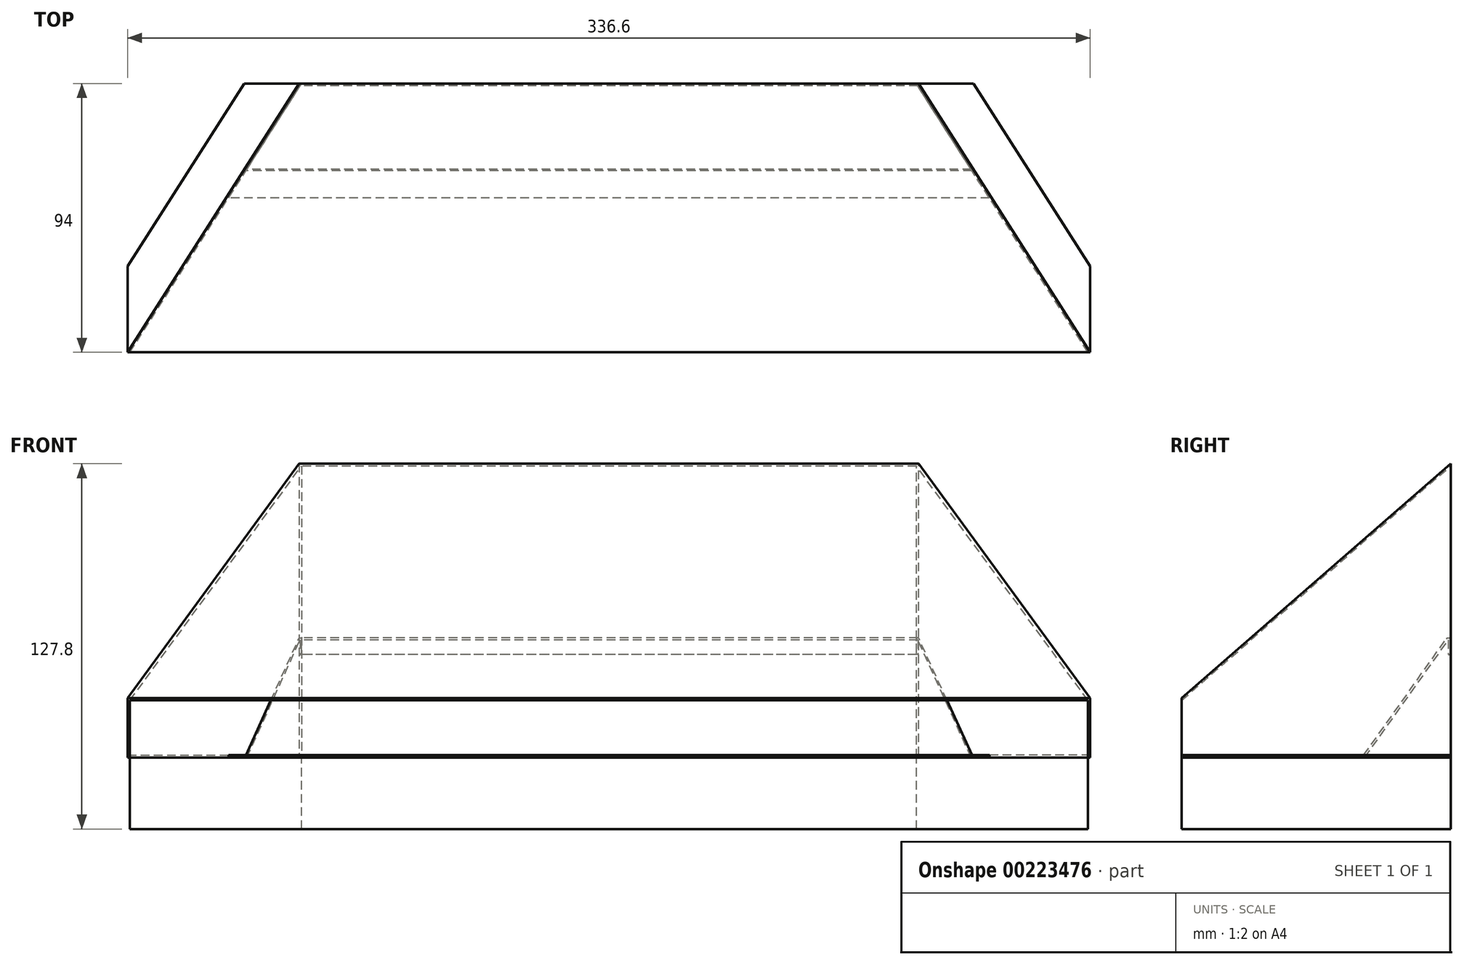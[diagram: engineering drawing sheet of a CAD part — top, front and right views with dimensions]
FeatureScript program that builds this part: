
annotation { "Feature Type Name" : "Feature", "Feature Type Description" : "" }
export const myFeature = defineFeature(function(context is Context, id is Id, definition is map)
    precondition{}
    {
        {
            var Q0;
            Q0=qCreatedBy(makeId("Front.planeOp"),FACE);
            var sketch = newSketch(context, id + "F0", { "sketchPlane" : qUnion([Q0])});
            skLineSegment(sketch, "E0.top", {"start": v(-167.5, 20) * mm, "end": v(167.5, 20) * mm});
            skLineSegment(sketch, "E0.left", {"start": v(-167.5, 0) * mm, "end": v(-167.5, 20) * mm});
            skLineSegment(sketch, "E0.right", {"start": v(167.5, 0) * mm, "end": v(167.5, 20) * mm});
            skLineSegment(sketch, "E1", {"start": v(-167.5, 0) * mm, "end": v(-187.5, 0) * mm});
            skLineSegment(sketch, "E2", {"start": v(167.5, 0) * mm, "end": v(187.5, 0) * mm});
            skLineSegment(sketch, "E3.0", {"start": v(-168.3, 0.8) * mm, "end": v(-187.5, 0.8) * mm});
            skLineSegment(sketch, "E3.1", {"start": v(168.3, 0.8) * mm, "end": v(187.5, 0.8) * mm});
            skLineSegment(sketch, "E3.2", {"start": v(168.3, 0.8) * mm, "end": v(168.3, 20.8) * mm});
            skLineSegment(sketch, "E3.3", {"start": v(-168.3, 20.8) * mm, "end": v(168.3, 20.8) * mm});
            skLineSegment(sketch, "E3.4", {"start": v(-168.3, 0.8) * mm, "end": v(-168.3, 20.8) * mm});
            skLineSegment(sketch, "E4", {"start": v(-187.5, 0.8) * mm, "end": v(-187.5, 0) * mm});
            skLineSegment(sketch, "E5", {"start": v(187.5, 0.8) * mm, "end": v(187.5, 0) * mm});
            skLineSegment(sketch, "E6.bottom", {"start": v(189, 0) * mm, "end": v(-189, 0) * mm, "construction": true});
            skLineSegment(sketch, "E6.top", {"start": v(189, 200.63) * mm, "end": v(-189, 200.63) * mm, "construction": true});
            skLineSegment(sketch, "E6.left", {"start": v(189, 0) * mm, "end": v(189, 200.63) * mm, "construction": true});
            skLineSegment(sketch, "E6.right", {"start": v(-189, 0) * mm, "end": v(-189, 200.63) * mm, "construction": true});
            skPoint(sketch, "E6.middle", {"position": v(0, 100.31) * mm});
            skSolve(sketch);
        }
        {
            var Q0;
            Q0=qCreatedBy(makeId("Right.planeOp"),FACE);
            var sketch = newSketch(context, id + "F1", { "sketchPlane" : qUnion([Q0])});
            skLineSegment(sketch, "E7", {"start": v(0, 0) * mm, "end": v(94, 0) * mm, "construction": true});
            skSolve(sketch);
        }
        {
            var Q0;
            Q0=sQuery(id+"F1.wireOp",VERTEX,"E7.end");
            var Q1;
            Q1=qCreatedBy(makeId("Front.planeOp"),FACE);
            cPlane(context, id + "F2", {"entities" : qUnion([Q0, Q1]), "cplaneType" : CPlaneType.PLANE_POINT, "offset" : 25 * mm, "width" : 150 * mm, "height" : 150 * mm});
        }
        {
            var Q0;
            Q0=qCreatedBy(id+"F2.planeOp",FACE);
            var sketch = newSketch(context, id + "F3", { "sketchPlane" : qUnion([Q0])});
            skLineSegment(sketch, "E8", {"start": v(127.5, 0) * mm, "end": v(107.5, 0) * mm});
            skLineSegment(sketch, "E9", {"start": v(107.5, 0) * mm, "end": v(107.5, 102) * mm});
            skLineSegment(sketch, "E10", {"start": v(107.5, 102) * mm, "end": v(-107.5, 102) * mm});
            skLineSegment(sketch, "E11", {"start": v(-107.5, 102) * mm, "end": v(-107.5, 0) * mm});
            skLineSegment(sketch, "E12", {"start": v(-107.5, 0) * mm, "end": v(-127.5, 0) * mm});
            skLineSegment(sketch, "E13.0", {"start": v(-108.3, 0.8) * mm, "end": v(-127.5, 0.8) * mm});
            skLineSegment(sketch, "E13.1", {"start": v(127.5, 0.8) * mm, "end": v(108.3, 0.8) * mm});
            skLineSegment(sketch, "E13.2", {"start": v(108.3, 0.8) * mm, "end": v(108.3, 102.8) * mm});
            skLineSegment(sketch, "E13.3", {"start": v(108.3, 102.8) * mm, "end": v(-108.3, 102.8) * mm});
            skLineSegment(sketch, "E13.4", {"start": v(-108.3, 102.8) * mm, "end": v(-108.3, 0.8) * mm});
            skLineSegment(sketch, "E14", {"start": v(-127.5, 0.81) * mm, "end": v(-127.5, 0) * mm});
            skLineSegment(sketch, "E15", {"start": v(127.5, 0.8) * mm, "end": v(127.5, 0) * mm});
            skSolve(sketch);
        }
        {
            var Q0;
            Q0=makeQuery(id+"F0.imprint","IMPRINT",FACE,{"disambiguationData":[TD([[makeQuery(id+"F0.imprint","IMPRINT",EDGE,{"derivedFrom":sQuery(id+"F0.wireOp",EDGE,"E0.top")}),1.0]])]});
            var Q1;
            Q1=makeQuery(id+"F3.imprint","IMPRINT",FACE,{"disambiguationData":[TD([[makeQuery(id+"F3.imprint","IMPRINT",EDGE,{"derivedFrom":sQuery(id+"F3.wireOp",EDGE,"E8")}),-1.0]])]});
            loft(context, id + "F4", {"sheetProfilesArray" : [{ "sheetProfileEntities" : qUnion([Q0]) }, { "sheetProfileEntities" : qUnion([Q1]) }]});
        }
        {
            var Q0;
            Q0=makeQuery(id+"F4.opLoft","SWEPT_FACE",FACE,{"disambiguationData":[OSD([sQuery(id+"F0.wireOp",EDGE,"E3.2"),sQuery(id+"F0.wireOp",EDGE,"E3.3"),sQuery(id+"F0.wireOp",EDGE,"E3.4"),sQuery(id+"F3.wireOp",EDGE,"E13.2"),sQuery(id+"F3.wireOp",EDGE,"E13.3"),sQuery(id+"F3.wireOp",EDGE,"E13.4")])]});
            var sketch = newSketch(context, id + "F5", { "sketchPlane" : qUnion([Q0])});
            skLineSegment(sketch, "E16.0", {"start": v(-168.3, 13.67) * mm, "end": v(-108.3, 138.41) * mm});
            skLineSegment(sketch, "E16.1", {"start": v(-168.3, 13.67) * mm, "end": v(168.3, 13.67) * mm});
            skLineSegment(sketch, "E16.2", {"start": v(168.3, 13.67) * mm, "end": v(108.3, 138.41) * mm});
            skLineSegment(sketch, "E16.3", {"start": v(-108.3, 138.41) * mm, "end": v(108.3, 138.41) * mm});
            skSolve(sketch);
        }
        {
            var Q0;
            Q0=makeQuery(id+"F4.opLoft","SWEPT_FACE",FACE,{"disambiguationData":[OSD([sQuery(id+"F0.wireOp",EDGE,"E3.0"),sQuery(id+"F0.wireOp",EDGE,"E3.4"),sQuery(id+"F0.wireOp",EDGE,"E4"),sQuery(id+"F3.wireOp",EDGE,"E13.0"),sQuery(id+"F3.wireOp",EDGE,"E13.4"),sQuery(id+"F3.wireOp",EDGE,"E14")])]});
            var sketch = newSketch(context, id + "F6", { "sketchPlane" : qUnion([Q0])});
            skLineSegment(sketch, "E17", {"start": v(-168.3, 0) * mm, "end": v(-168.3, 30.08) * mm});
            skLineSegment(sketch, "E18.0", {"start": v(168.3, 0) * mm, "end": v(187.5, 0) * mm});
            skLineSegment(sketch, "E18.1", {"start": v(187.5, 0) * mm, "end": v(127.5, 94) * mm});
            skLineSegment(sketch, "E18.2", {"start": v(168.3, 0) * mm, "end": v(108.3, 94) * mm});
            skLineSegment(sketch, "E19", {"start": v(168.3, 0) * mm, "end": v(168.3, 30.08) * mm});
            skSolve(sketch);
        }
        {
            var Q0;
            {var subQ0=sQuery(id+"F6.wireOp",EDGE,"E17");Q0=makeQuery(id+"F6.imprint","IMPRINT",FACE,{"disambiguationData":[TD([[makeQuery(id+"F6.imprint","IMPRINT",EDGE,{"derivedFrom":subQ0}),1.0]])]});}
            var Q1;
            {var subQ0=sQuery(id+"F6.wireOp",EDGE,"E18.0");Q1=makeQuery(id+"F6.imprint","IMPRINT",FACE,{"disambiguationData":[TD([[makeQuery(id+"F6.imprint","IMPRINT",EDGE,{"derivedFrom":subQ0}),1.0]])]});}
            extrude(context, id + "F7", {"entities" : qUnion([Q0, Q1]), "operationType" : NewBodyOperationType.REMOVE, "endBound" : BoundingType.THROUGH_ALL, "oppositeDirection" : true, "depth" : 25 * mm});
        }
        {
            var Q0;
            Q0=makeQuery(id+"F4.opLoft","SWEPT_FACE",FACE,{"disambiguationData":[OSD([sQuery(id+"F0.wireOp",EDGE,"E3.0"),sQuery(id+"F0.wireOp",EDGE,"E3.3"),sQuery(id+"F0.wireOp",EDGE,"E3.4"),sQuery(id+"F3.wireOp",EDGE,"E13.0"),sQuery(id+"F3.wireOp",EDGE,"E13.3"),sQuery(id+"F3.wireOp",EDGE,"E13.4")])]});
            var sketch = newSketch(context, id + "F8", { "sketchPlane" : qUnion([Q0])});
            skLineSegment(sketch, "E20.0", {"start": v(90.55, 20.8) * mm, "end": v(-20.97, 102.8) * mm});
            skLineSegment(sketch, "E20.1", {"start": v(90.55, 0.8) * mm, "end": v(90.55, 20.8) * mm});
            skLineSegment(sketch, "E20.2", {"start": v(-20.97, 0.8) * mm, "end": v(-20.97, 102.8) * mm});
            skLineSegment(sketch, "E20.3", {"start": v(90.55, 0.8) * mm, "end": v(-20.97, 0.8) * mm});
            skSolve(sketch);
        }
        {
            var Q0;
            Q0=qCreatedBy(makeId("Right.planeOp"),FACE);
            var sketch = newSketch(context, id + "F9", { "sketchPlane" : qUnion([Q0])});
            skLineSegment(sketch, "E21", {"start": v(93.2, 41.13) * mm, "end": v(64, 0) * mm});
            skLineSegment(sketch, "E22", {"start": v(64, 0) * mm, "end": v(54, 0) * mm});
            skLineSegment(sketch, "E23.0", {"start": v(63.59, 0.8) * mm, "end": v(54, 0.8) * mm});
            skLineSegment(sketch, "E23.1", {"start": v(92.55, 41.6) * mm, "end": v(63.59, 0.8) * mm});
            skLineSegment(sketch, "E24", {"start": v(54, 0.8) * mm, "end": v(54, 0) * mm});
            skPoint(sketch, "E25.orphan", {"position": v(94, 0.8) * mm});
            skPoint(sketch, "E26.orphan", {"position": v(94, 102.8) * mm});
            skLineSegment(sketch, "E27", {"start": v(94, 41.13) * mm, "end": v(94, 36.1) * mm});
            skLineSegment(sketch, "E28", {"start": v(94, 36.1) * mm, "end": v(93.2, 36.1) * mm});
            skLineSegment(sketch, "E29", {"start": v(93.2, 36.1) * mm, "end": v(93.2, 41.13) * mm});
            skPoint(sketch, "E30.orphan", {"position": v(94, 42.26) * mm});
            skPoint(sketch, "E31.visualSharp", {"position": v(93.2, 41.13) * mm});
            skLineSegment(sketch, "E31.filletArc", {"start": v(93.2, 41.13) * mm, "end": v(93.2, 41.13) * mm});
            skPoint(sketch, "E32.visualSharp", {"position": v(94, 43.64) * mm});
            skArc(sketch, "E32.filletArc", {"start": v(94, 41.13) * mm, "mid": v(93.44, 41.9) * mm, "end": v(92.55, 41.6) * mm});
            skSolve(sketch);
        }
        {
            var Q0;
            Q0=makeQuery(id+"F9.imprint","IMPRINT",FACE,{"disambiguationData":[TD([[makeQuery(id+"F9.imprint","IMPRINT",EDGE,{"derivedFrom":sQuery(id+"F9.wireOp",EDGE,"E21")}),-1.0]])]});
            var Q1;
            Q1=makeQuery(id+"F4.opLoft","SWEPT_FACE",FACE,{"disambiguationData":[OSD([sQuery(id+"F0.wireOp",EDGE,"E0.top"),sQuery(id+"F0.wireOp",EDGE,"E0.right"),sQuery(id+"F0.wireOp",EDGE,"E2"),sQuery(id+"F3.wireOp",EDGE,"E8"),sQuery(id+"F3.wireOp",EDGE,"E9"),sQuery(id+"F3.wireOp",EDGE,"E10")])]});
            var Q2;
            Q2=makeQuery(id+"F4.opLoft","SWEPT_FACE",FACE,{"disambiguationData":[OSD([sQuery(id+"F0.wireOp",EDGE,"E0.top"),sQuery(id+"F0.wireOp",EDGE,"E0.left"),sQuery(id+"F0.wireOp",EDGE,"E1"),sQuery(id+"F3.wireOp",EDGE,"E10"),sQuery(id+"F3.wireOp",EDGE,"E11"),sQuery(id+"F3.wireOp",EDGE,"E12")])]});
            extrude(context, id + "F10", {"entities" : qUnion([Q0]), "endBound" : BoundingType.UP_TO_SURFACE, "endBoundEntityFace" : qUnion([Q1]), "depth" : 25 * mm, "hasSecondDirection" : true, "secondDirectionBound" : SecondDirectionBoundingType.UP_TO_SURFACE, "secondDirectionOppositeDirection" : true, "secondDirectionBoundEntityFace" : qUnion([Q2]), "secondDirectionDepth" : 25 * mm});
        }
        {
            var Q0;
            Q0=makeQuery(id+"F4.opLoft","SWEPT_FACE",FACE,{"disambiguationData":[OSD([sQuery(id+"F0.wireOp",EDGE,"E0.right"),sQuery(id+"F0.wireOp",EDGE,"E2"),sQuery(id+"F0.wireOp",EDGE,"E5"),sQuery(id+"F3.wireOp",EDGE,"E8"),sQuery(id+"F3.wireOp",EDGE,"E9"),sQuery(id+"F3.wireOp",EDGE,"E15")])]});
            var sketch = newSketch(context, id + "F11", { "sketchPlane" : qUnion([Q0])});
            skLineSegment(sketch, "E33.0", {"start": v(167.5, 0) * mm, "end": v(-167.5, 0) * mm});
            skLineSegment(sketch, "E33.1", {"start": v(167.5, 0) * mm, "end": v(107.5, -94) * mm});
            skLineSegment(sketch, "E33.2", {"start": v(107.5, -94) * mm, "end": v(-107.5, -94) * mm});
            skLineSegment(sketch, "E33.3", {"start": v(-167.5, 0) * mm, "end": v(-107.5, -94) * mm});
            skSolve(sketch);
        }
        {
            var Q0;
            Q0 = qSketchRegion(id + "F11", true);
            extrude(context, id + "F12", {"entities" : qUnion([Q0]), "depth" : 25 * mm});
        }
    });
